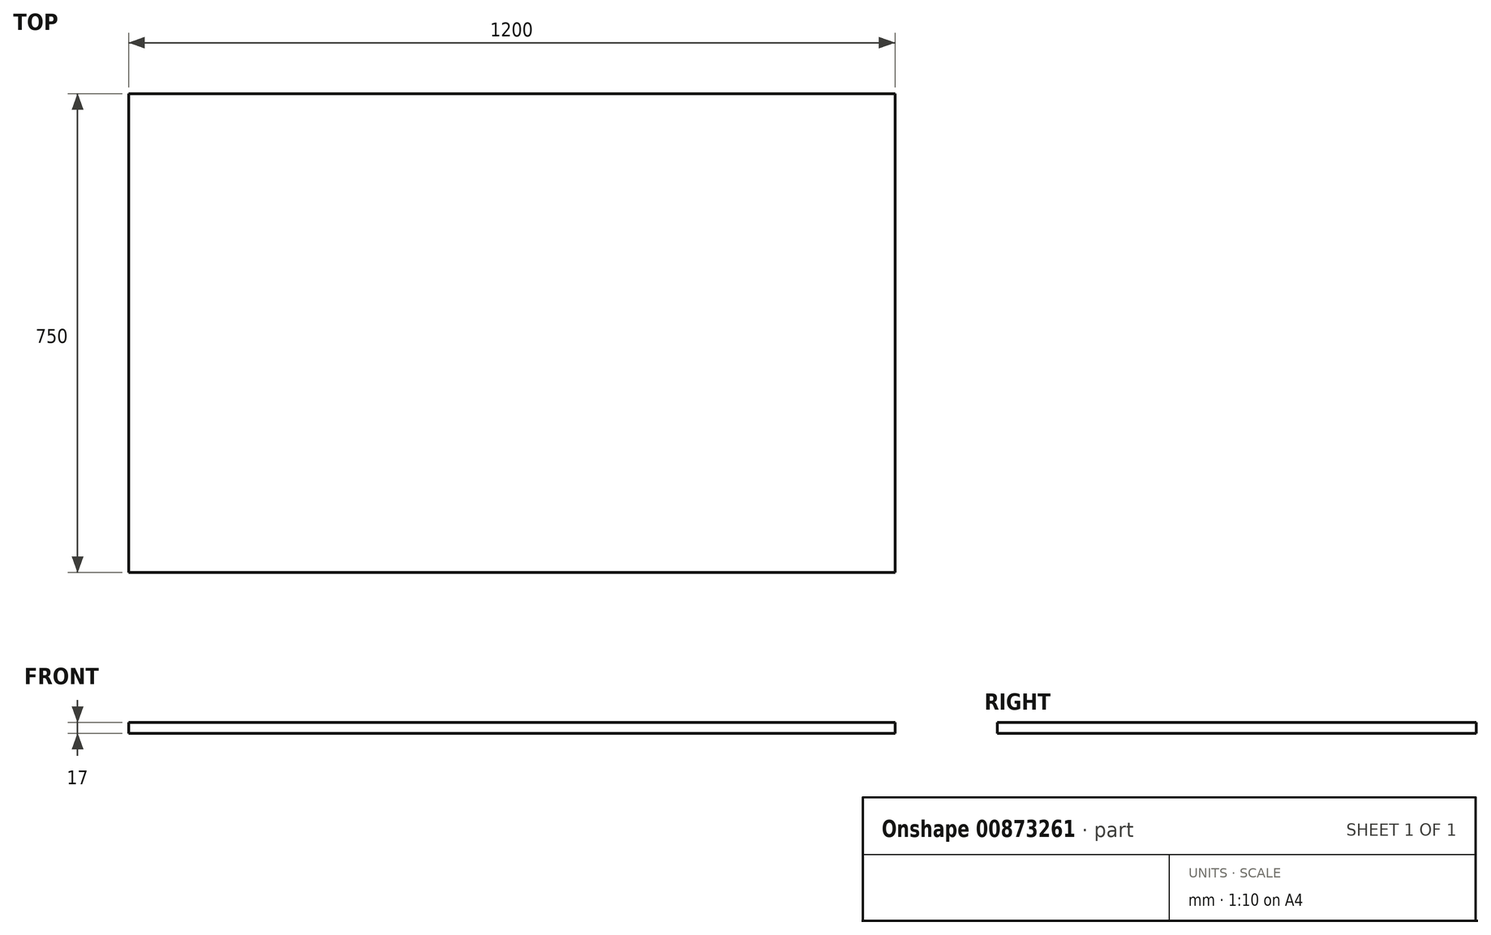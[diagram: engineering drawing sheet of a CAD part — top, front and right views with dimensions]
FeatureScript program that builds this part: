
annotation { "Feature Type Name" : "Feature", "Feature Type Description" : "" }
export const myFeature = defineFeature(function(context is Context, id is Id, definition is map)
    precondition{}
    {
        {
            var Q0;
            Q0=qCreatedBy(makeId("Front.planeOp"),FACE);
            var sketch = newSketch(context, id + "F0", { "sketchPlane" : qUnion([Q0])});
            skLineSegment(sketch, "E0.bottom", {"start": v(548.17, -8.5) * mm, "end": v(-651.83, -8.5) * mm});
            skLineSegment(sketch, "E0.top", {"start": v(548.17, 8.5) * mm, "end": v(-651.83, 8.5) * mm});
            skLineSegment(sketch, "E0.left", {"start": v(548.17, -8.5) * mm, "end": v(548.17, 8.5) * mm});
            skLineSegment(sketch, "E0.right", {"start": v(-651.83, -8.5) * mm, "end": v(-651.83, 8.5) * mm});
            skPoint(sketch, "E0.middle", {"position": v(-51.83, 0) * mm});
            skSolve(sketch);
        }
        {
            var Q0;
            Q0=makeQuery(id+"F0.imprint","IMPRINT",FACE,{"disambiguationData":[TD([[makeQuery(id+"F0.imprint","IMPRINT",EDGE,{"derivedFrom":sQuery(id+"F0.wireOp",EDGE,"E0.bottom")}),-1.0]])]});
            extrude(context, id + "F1", {"entities" : qUnion([Q0]), "endBound" : BoundingType.SYMMETRIC, "depth" : 750 * mm, "offsetDistance" : 25 * mm});
        }
        {
            var Q0;
            Q0=qCreatedBy(makeId("Right.planeOp"),FACE);
            var sketch = newSketch(context, id + "F2", { "sketchPlane" : qUnion([Q0])});
            skLineSegment(sketch, "E1.bottom", {"start": v(-374.49, -9.62) * mm, "end": v(-329.49, -9.62) * mm});
            skLineSegment(sketch, "E1.top", {"start": v(-374.49, -99.62) * mm, "end": v(-329.49, -99.62) * mm});
            skLineSegment(sketch, "E1.left", {"start": v(-374.49, -9.62) * mm, "end": v(-374.49, -99.62) * mm});
            skLineSegment(sketch, "E1.right", {"start": v(-329.49, -9.62) * mm, "end": v(-329.49, -99.62) * mm});
            skSolve(sketch);
        }
        {
            var Q0;
            Q0 = qSketchRegion(id + "F2", true);
            extrude(context, id + "F3", {"entities" : qUnion([Q0]), "endBound" : BoundingType.SYMMETRIC, "depth" : 1696 * mm, "offsetDistance" : 25 * mm});
        }
        {
            var Q0;
            Q0=makeQuery(id+"F3.opExtrude","SWEPT_BODY",BODY,{"disambiguationData":[OSD([sQuery(id+"F2.wireOp",EDGE,"E1.bottom"),sQuery(id+"F2.wireOp",EDGE,"E1.top"),sQuery(id+"F2.wireOp",EDGE,"E1.left"),sQuery(id+"F2.wireOp",EDGE,"E1.right")])]});
            deleteBodies(context, id + "F4", {"entities" : qUnion([Q0])});
        }
        {
            var Q0;
            Q0=makeQuery(id+"F1.opExtrude","SWEPT_FACE",FACE,{"disambiguationData":[OSD([sQuery(id+"F0.wireOp",EDGE,"E0.left")])]});
            var sketch = newSketch(context, id + "F5", { "sketchPlane" : qUnion([Q0])});
            skLineSegment(sketch, "E2.bottom", {"start": v(-375, -8.6) * mm, "end": v(-330, -8.6) * mm});
            skLineSegment(sketch, "E2.top", {"start": v(-375, -98.6) * mm, "end": v(-330, -98.6) * mm});
            skLineSegment(sketch, "E2.left", {"start": v(-375, -8.6) * mm, "end": v(-375, -98.6) * mm});
            skLineSegment(sketch, "E2.right", {"start": v(-330, -8.6) * mm, "end": v(-330, -98.6) * mm});
            skLineSegment(sketch, "E3", {"start": v(-375, -8.5) * mm, "end": v(-375, -8.6) * mm});
            skSolve(sketch);
        }
        {
            var Q0;
            Q0=makeQuery(id+"F5.imprint","IMPRINT",FACE,{"disambiguationData":[TD([[makeQuery(id+"F5.imprint","IMPRINT",EDGE,{"derivedFrom":sQuery(id+"F5.wireOp",EDGE,"E2.bottom")}),-1.0]])]});
            extrude(context, id + "F6", {"entities" : qUnion([Q0]), "oppositeDirection" : true, "depth" : 1800 * mm, "offsetDistance" : 25 * mm});
        }
        {
            var Q0;
            Q0=makeQuery(id+"F6.opExtrude","SWEPT_BODY",BODY,{"disambiguationData":[OSD([sQuery(id+"F5.wireOp",EDGE,"E2.bottom"),sQuery(id+"F5.wireOp",EDGE,"E2.top"),sQuery(id+"F5.wireOp",EDGE,"E2.left"),sQuery(id+"F5.wireOp",EDGE,"E2.right")])]});
            deleteBodies(context, id + "F7", {"entities" : qUnion([Q0])});
        }
    });
